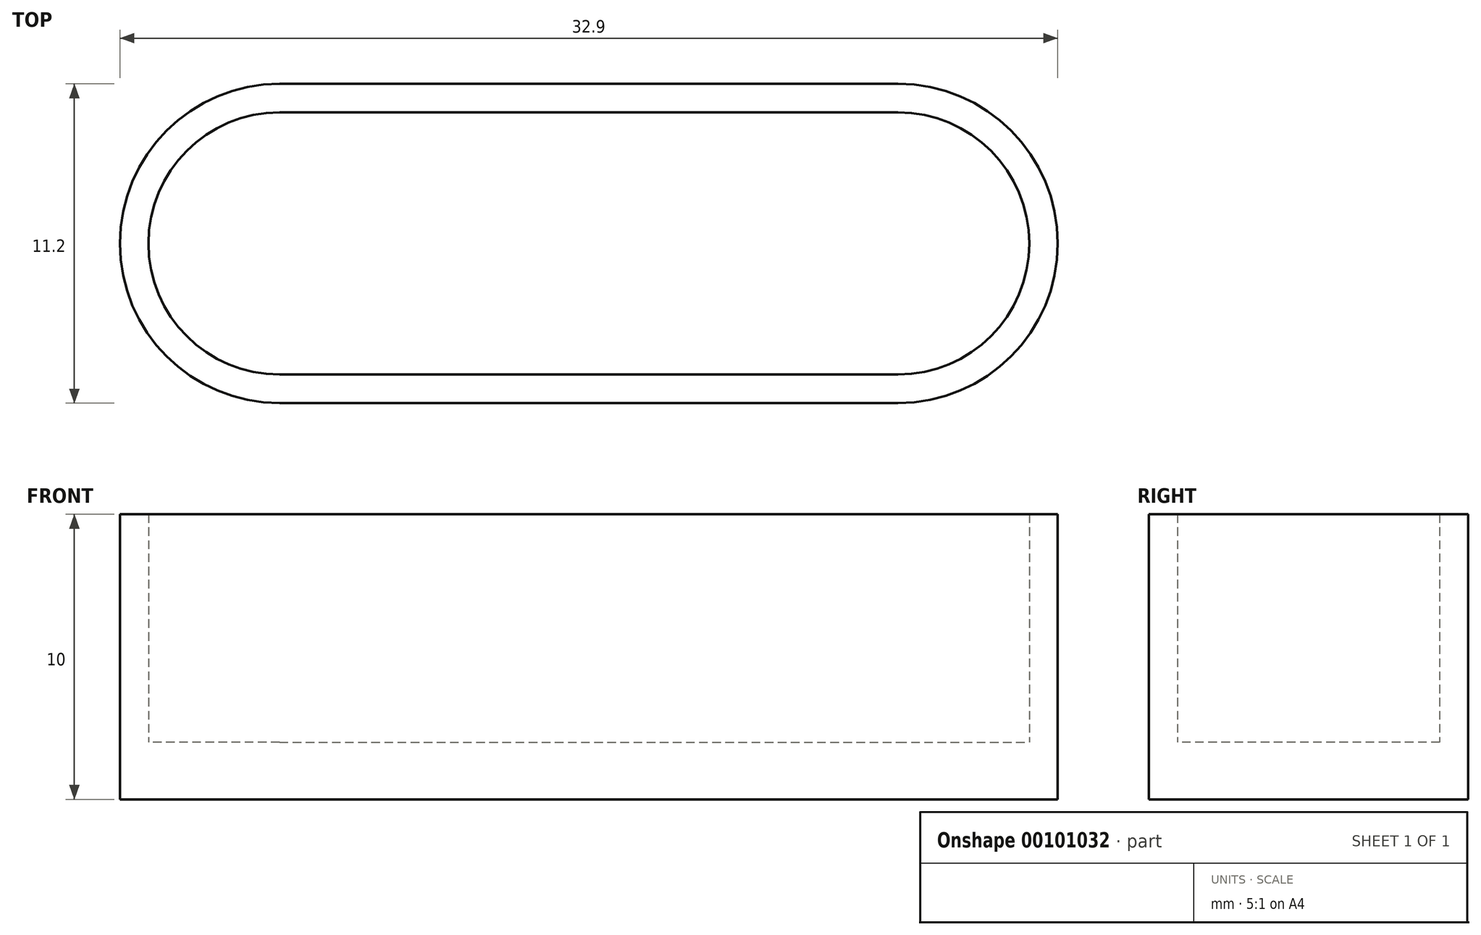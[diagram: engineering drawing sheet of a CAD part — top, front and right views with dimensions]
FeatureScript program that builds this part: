
annotation { "Feature Type Name" : "Feature", "Feature Type Description" : "" }
export const myFeature = defineFeature(function(context is Context, id is Id, definition is map)
    precondition{}
    {
        {
            var Q0;
            Q0=qCreatedBy(makeId("Top.planeOp"),FACE);
            var sketch = newSketch(context, id + "F0", { "sketchPlane" : qUnion([Q0])});
            skLineSegment(sketch, "E0.bottom", {"start": v(-10.85, 4.6) * mm, "end": v(10.85, 4.6) * mm, "construction": true});
            skLineSegment(sketch, "E0.top", {"start": v(-10.85, -4.6) * mm, "end": v(10.85, -4.6) * mm, "construction": true});
            skPoint(sketch, "E0.middle", {"position": v(0, 0) * mm});
            skLineSegment(sketch, "E1", {"start": v(-15.45, 0) * mm, "end": v(-10.85, 0) * mm});
            skPoint(sketch, "E1.endSnap0", {"position": v(-15.45, 0) * mm});
            skArc(sketch, "E2", {"start": v(-10.85, 4.6) * mm, "mid": v(-15.45, 0) * mm, "end": v(-10.85, -4.6) * mm, "construction": true});
            skArc(sketch, "E3.MirrorC", {"start": v(10.85, 4.6) * mm, "mid": v(15.45, 0) * mm, "end": v(10.85, -4.6) * mm, "construction": true});
            skPoint(sketch, "E0.left.start.orphan", {"position": v(-14.95, 4.6) * mm});
            skPoint(sketch, "E4.orphan", {"position": v(-15.95, -4.6) * mm});
            skPoint(sketch, "E5.orphan", {"position": v(15.95, 4.6) * mm});
            skPoint(sketch, "E0.right.end.orphan", {"position": v(14.95, -4.6) * mm});
            skLineSegment(sketch, "E6.0", {"start": v(-10.85, 5.6) * mm, "end": v(10.85, 5.6) * mm});
            skArc(sketch, "E6.1", {"start": v(-10.85, 5.6) * mm, "mid": v(-16.45, 0) * mm, "end": v(-10.85, -5.6) * mm});
            skLineSegment(sketch, "E6.2", {"start": v(-10.85, -5.6) * mm, "end": v(10.85, -5.6) * mm});
            skArc(sketch, "E6.3", {"start": v(10.85, 5.6) * mm, "mid": v(16.45, 0) * mm, "end": v(10.85, -5.6) * mm});
            skSolve(sketch);
        }
        {
            var Q0;
            Q0 = qSketchRegion(id + "F0", true);
            extrude(context, id + "F1", {"entities" : qUnion([Q0]), "depth" : 2 * mm});
        }
        {
            var Q0;
            Q0=makeQuery(id+"F1.opExtrude","CAP_FACE",FACE,{"disambiguationData":[OSD([sQuery(id+"F0.wireOp",EDGE,"E6.0"),sQuery(id+"F0.wireOp",EDGE,"E6.1"),sQuery(id+"F0.wireOp",EDGE,"E6.2"),sQuery(id+"F0.wireOp",EDGE,"E6.3")])],"isStart":false});
            var sketch = newSketch(context, id + "F2", { "sketchPlane" : qUnion([Q0])});
            skLineSegment(sketch, "E7.0", {"start": v(-10.85, 4.6) * mm, "end": v(10.85, 4.6) * mm});
            skArc(sketch, "E7.1", {"start": v(-10.85, 4.6) * mm, "mid": v(-15.45, 0) * mm, "end": v(-10.85, -4.6) * mm});
            skLineSegment(sketch, "E7.2", {"start": v(-10.85, -4.6) * mm, "end": v(10.85, -4.6) * mm});
            skArc(sketch, "E7.3", {"start": v(10.85, 4.6) * mm, "mid": v(15.45, 0) * mm, "end": v(10.85, -4.6) * mm});
            skArc(sketch, "E7.4", {"start": v(10.85, 5.6) * mm, "mid": v(16.45, 0) * mm, "end": v(10.85, -5.6) * mm});
            skLineSegment(sketch, "E7.5", {"start": v(-10.85, -5.6) * mm, "end": v(10.85, -5.6) * mm});
            skArc(sketch, "E7.6", {"start": v(-10.85, 5.6) * mm, "mid": v(-16.45, 0) * mm, "end": v(-10.85, -5.6) * mm});
            skLineSegment(sketch, "E7.7", {"start": v(-10.85, 5.6) * mm, "end": v(10.85, 5.6) * mm});
            skSolve(sketch);
        }
        {
            var Q0;
            Q0 = qSketchRegion(id + "F2", true);
            extrude(context, id + "F3", {"entities" : qUnion([Q0]), "operationType" : NewBodyOperationType.ADD, "depth" : 8 * mm});
        }
    });
